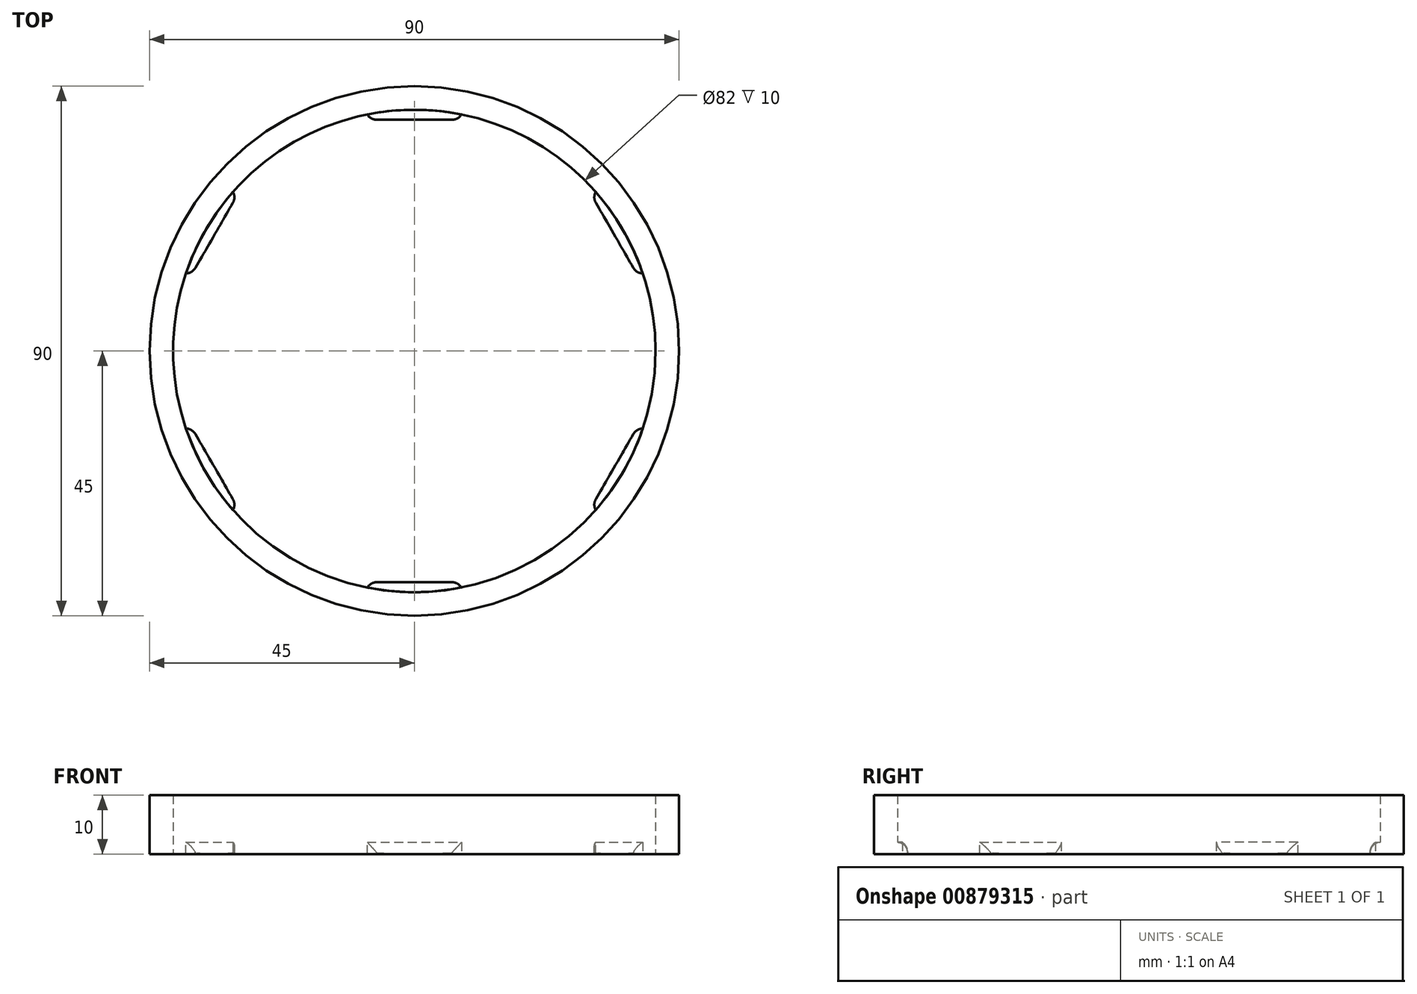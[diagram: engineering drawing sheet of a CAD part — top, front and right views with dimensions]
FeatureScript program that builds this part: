
annotation { "Feature Type Name" : "Feature", "Feature Type Description" : "" }
export const myFeature = defineFeature(function(context is Context, id is Id, definition is map)
    precondition{}
    {
        {
            var Q0;
            Q0=qCreatedBy(makeId("Top.planeOp"),FACE);
            var sketch = newSketch(context, id + "F0", { "sketchPlane" : qUnion([Q0])});
            skCircle(sketch, "E0", {"center": v(0, 0) * mm, "radius": 41 * mm});
            skLineSegment(sketch, "E1.top", {"start": v(30.03, 26.58) * mm, "end": v(34.03, 19.65) * mm});
            skPoint(sketch, "E1.middle", {"position": v(35.5, 20.5) * mm});
            skLineSegment(sketch, "E2", {"start": v(30.03, 26.58) * mm, "end": v(30.82, 27.03) * mm});
            skLineSegment(sketch, "E3.MirrorCS", {"start": v(38.03, 12.72) * mm, "end": v(38.82, 13.18) * mm});
            skLineSegment(sketch, "E4.MirrorCS", {"start": v(38.03, 12.72) * mm, "end": v(34.03, 19.65) * mm});
            skLineSegment(sketch, "E5.1.0", {"start": v(-8, 39.3) * mm, "end": v(-8, 40.21) * mm});
            skLineSegment(sketch, "E5.1.1", {"start": v(-8, 39.3) * mm, "end": v(0, 39.3) * mm});
            skLineSegment(sketch, "E5.1.2", {"start": v(8, 39.3) * mm, "end": v(0, 39.3) * mm});
            skLineSegment(sketch, "E5.1.3", {"start": v(8, 39.3) * mm, "end": v(8, 40.21) * mm});
            skLineSegment(sketch, "E5.2.0", {"start": v(-38.03, 12.72) * mm, "end": v(-38.82, 13.18) * mm});
            skLineSegment(sketch, "E5.2.1", {"start": v(-38.03, 12.72) * mm, "end": v(-34.03, 19.65) * mm});
            skLineSegment(sketch, "E5.2.2", {"start": v(-30.03, 26.58) * mm, "end": v(-34.03, 19.65) * mm});
            skLineSegment(sketch, "E5.2.3", {"start": v(-30.03, 26.58) * mm, "end": v(-30.82, 27.03) * mm});
            skLineSegment(sketch, "E5.3.0", {"start": v(-30.03, -26.58) * mm, "end": v(-30.82, -27.03) * mm});
            skLineSegment(sketch, "E5.3.1", {"start": v(-30.03, -26.58) * mm, "end": v(-34.03, -19.65) * mm});
            skLineSegment(sketch, "E5.3.2", {"start": v(-38.03, -12.72) * mm, "end": v(-34.03, -19.65) * mm});
            skLineSegment(sketch, "E5.3.3", {"start": v(-38.03, -12.72) * mm, "end": v(-38.82, -13.18) * mm});
            skLineSegment(sketch, "E5.4.0", {"start": v(8, -39.3) * mm, "end": v(8, -40.21) * mm});
            skLineSegment(sketch, "E5.4.1", {"start": v(8, -39.3) * mm, "end": v(0, -39.3) * mm});
            skLineSegment(sketch, "E5.4.2", {"start": v(-8, -39.3) * mm, "end": v(0, -39.3) * mm});
            skLineSegment(sketch, "E5.4.3", {"start": v(-8, -39.3) * mm, "end": v(-8, -40.21) * mm});
            skLineSegment(sketch, "E5.5.0", {"start": v(38.03, -12.72) * mm, "end": v(38.82, -13.18) * mm});
            skLineSegment(sketch, "E5.5.1", {"start": v(38.03, -12.72) * mm, "end": v(34.03, -19.65) * mm});
            skLineSegment(sketch, "E5.5.2", {"start": v(30.03, -26.58) * mm, "end": v(34.03, -19.65) * mm});
            skLineSegment(sketch, "E5.5.3", {"start": v(30.03, -26.58) * mm, "end": v(30.82, -27.03) * mm});
            skCircle(sketch, "E6", {"center": v(0, 0) * mm, "radius": 45 * mm});
            skSolve(sketch);
        }
        {
            var Q0;
            Q0=makeQuery(id+"F0.imprint","IMPRINT",FACE,{"disambiguationData":[TD([[makeQuery(id+"F0.imprint","IMPRINT",EDGE,{"derivedFrom":sQuery(id+"F0.wireOp",EDGE,"E6")}),1.0]])]});
            extrude(context, id + "F1", {"entities" : qUnion([Q0]), "depth" : 10 * mm, "offsetDistance" : 25 * mm});
        }
        {
            var Q0;
            {var subQ0=sQuery(id+"F0.wireOp",EDGE,"E5.1.0");Q0=makeQuery(id+"F0.imprint","IMPRINT",FACE,{"disambiguationData":[TD([[makeQuery(id+"F0.imprint","IMPRINT",EDGE,{"derivedFrom":subQ0}),-1.0]])]});}
            var Q1;
            {var subQ0=sQuery(id+"F0.wireOp",EDGE,"E5.2.0");Q1=makeQuery(id+"F0.imprint","IMPRINT",FACE,{"disambiguationData":[TD([[makeQuery(id+"F0.imprint","IMPRINT",EDGE,{"derivedFrom":subQ0}),-1.0]])]});}
            var Q2;
            Q2=makeQuery(id+"F0.imprint","IMPRINT",FACE,{"disambiguationData":[TD([[makeQuery(id+"F0.imprint","IMPRINT",EDGE,{"derivedFrom":sQuery(id+"F0.wireOp",EDGE,"E1.top")}),1.0]])]});
            var Q3;
            {var subQ0=sQuery(id+"F0.wireOp",EDGE,"E5.5.0");Q3=makeQuery(id+"F0.imprint","IMPRINT",FACE,{"disambiguationData":[TD([[makeQuery(id+"F0.imprint","IMPRINT",EDGE,{"derivedFrom":subQ0}),-1.0]])]});}
            var Q4;
            {var subQ0=sQuery(id+"F0.wireOp",EDGE,"E5.4.0");Q4=makeQuery(id+"F0.imprint","IMPRINT",FACE,{"disambiguationData":[TD([[makeQuery(id+"F0.imprint","IMPRINT",EDGE,{"derivedFrom":subQ0}),-1.0]])]});}
            var Q5;
            {var subQ0=sQuery(id+"F0.wireOp",EDGE,"E5.3.0");Q5=makeQuery(id+"F0.imprint","IMPRINT",FACE,{"disambiguationData":[TD([[makeQuery(id+"F0.imprint","IMPRINT",EDGE,{"derivedFrom":subQ0}),-1.0]])]});}
            extrude(context, id + "F2", {"entities" : qUnion([Q0, Q1, Q2, Q3, Q4, Q5]), "operationType" : NewBodyOperationType.ADD, "depth" : 2 * mm, "offsetDistance" : 25 * mm});
        }
        {
            var Q0;
            Q0=makeQuery(id+"F2.opExtrude","CAP_EDGE",EDGE,{"disambiguationData":[OSD([sQuery(id+"F0.wireOp",EDGE,"E5.1.1"),sQuery(id+"F0.wireOp",EDGE,"E5.1.2")])],"isStart":false});
            var Q1;
            Q1=makeQuery(id+"F2.opExtrude","SWEPT_EDGE",EDGE,{"disambiguationData":[OSD([sQuery(id+"F0.wireOp",EDGE,"E5.1.2"),sQuery(id+"F0.wireOp",EDGE,"E5.1.3")])]});
            var Q2;
            Q2=makeQuery(id+"F2.opExtrude","SWEPT_EDGE",EDGE,{"disambiguationData":[OSD([sQuery(id+"F0.wireOp",EDGE,"E5.1.0"),sQuery(id+"F0.wireOp",EDGE,"E5.1.1")])]});
            fillet(context, id + "F3", {"entities" : qUnion([Q0, Q1, Q2]), "radius" : 2 * mm, "tangentPropagation" : true, "rho" : 0.5, "crossSection" : FilletCrossSection.CONIC, "allowEdgeOverflow" : false});
        }
        {
            var Q0;
            Q0=makeQuery(id+"F2.opExtrude","CAP_EDGE",EDGE,{"disambiguationData":[OSD([sQuery(id+"F0.wireOp",EDGE,"E5.2.1"),sQuery(id+"F0.wireOp",EDGE,"E5.2.2")])],"isStart":false});
            var Q1;
            Q1=makeQuery(id+"F2.opExtrude","SWEPT_EDGE",EDGE,{"disambiguationData":[OSD([sQuery(id+"F0.wireOp",EDGE,"E5.2.0"),sQuery(id+"F0.wireOp",EDGE,"E5.2.1")])]});
            var Q2;
            Q2=makeQuery(id+"F2.opExtrude","SWEPT_EDGE",EDGE,{"disambiguationData":[OSD([sQuery(id+"F0.wireOp",EDGE,"E5.2.2"),sQuery(id+"F0.wireOp",EDGE,"E5.2.3")])]});
            fillet(context, id + "F4", {"entities" : qUnion([Q0, Q1, Q2]), "radius" : 2 * mm, "tangentPropagation" : true, "rho" : 0.5, "crossSection" : FilletCrossSection.CONIC, "allowEdgeOverflow" : false});
        }
        {
            var Q0;
            Q0=makeQuery(id+"F2.opExtrude","CAP_EDGE",EDGE,{"disambiguationData":[OSD([sQuery(id+"F0.wireOp",EDGE,"E5.3.1"),sQuery(id+"F0.wireOp",EDGE,"E5.3.2")])],"isStart":false});
            var Q1;
            Q1=makeQuery(id+"F2.opExtrude","SWEPT_EDGE",EDGE,{"disambiguationData":[OSD([sQuery(id+"F0.wireOp",EDGE,"E5.3.0"),sQuery(id+"F0.wireOp",EDGE,"E5.3.1")])]});
            var Q2;
            Q2=makeQuery(id+"F2.opExtrude","SWEPT_EDGE",EDGE,{"disambiguationData":[OSD([sQuery(id+"F0.wireOp",EDGE,"E5.3.2"),sQuery(id+"F0.wireOp",EDGE,"E5.3.3")])]});
            fillet(context, id + "F5", {"entities" : qUnion([Q0, Q1, Q2]), "radius" : 2 * mm, "tangentPropagation" : true, "rho" : 0.5, "crossSection" : FilletCrossSection.CONIC, "allowEdgeOverflow" : false});
        }
        {
            var Q0;
            Q0=makeQuery(id+"F2.opExtrude","CAP_EDGE",EDGE,{"disambiguationData":[OSD([sQuery(id+"F0.wireOp",EDGE,"E5.4.1"),sQuery(id+"F0.wireOp",EDGE,"E5.4.2")])],"isStart":false});
            var Q1;
            Q1=makeQuery(id+"F2.opExtrude","SWEPT_EDGE",EDGE,{"disambiguationData":[OSD([sQuery(id+"F0.wireOp",EDGE,"E5.4.2"),sQuery(id+"F0.wireOp",EDGE,"E5.4.3")])]});
            var Q2;
            Q2=makeQuery(id+"F2.opExtrude","SWEPT_EDGE",EDGE,{"disambiguationData":[OSD([sQuery(id+"F0.wireOp",EDGE,"E5.4.0"),sQuery(id+"F0.wireOp",EDGE,"E5.4.1")])]});
            fillet(context, id + "F6", {"entities" : qUnion([Q0, Q1, Q2]), "radius" : 2 * mm, "tangentPropagation" : true, "rho" : 0.5, "crossSection" : FilletCrossSection.CONIC, "allowEdgeOverflow" : false});
        }
        {
            var Q0;
            Q0=makeQuery(id+"F2.opExtrude","CAP_EDGE",EDGE,{"disambiguationData":[OSD([sQuery(id+"F0.wireOp",EDGE,"E5.5.1"),sQuery(id+"F0.wireOp",EDGE,"E5.5.2")])],"isStart":false});
            var Q1;
            Q1=makeQuery(id+"F2.opExtrude","SWEPT_EDGE",EDGE,{"disambiguationData":[OSD([sQuery(id+"F0.wireOp",EDGE,"E5.5.2"),sQuery(id+"F0.wireOp",EDGE,"E5.5.3")])]});
            var Q2;
            Q2=makeQuery(id+"F2.opExtrude","SWEPT_EDGE",EDGE,{"disambiguationData":[OSD([sQuery(id+"F0.wireOp",EDGE,"E5.5.0"),sQuery(id+"F0.wireOp",EDGE,"E5.5.1")])]});
            fillet(context, id + "F7", {"entities" : qUnion([Q0, Q1, Q2]), "radius" : 2 * mm, "tangentPropagation" : true, "rho" : 0.5, "crossSection" : FilletCrossSection.CONIC, "allowEdgeOverflow" : false});
        }
        {
            var Q0;
            Q0=makeQuery(id+"F2.opExtrude","CAP_EDGE",EDGE,{"disambiguationData":[OSD([sQuery(id+"F0.wireOp",EDGE,"E1.top"),sQuery(id+"F0.wireOp",EDGE,"E4.MirrorCS")])],"isStart":false});
            var Q1;
            Q1=makeQuery(id+"F2.opExtrude","SWEPT_EDGE",EDGE,{"disambiguationData":[OSD([sQuery(id+"F0.wireOp",EDGE,"E1.top"),sQuery(id+"F0.wireOp",EDGE,"E2")])]});
            var Q2;
            Q2=makeQuery(id+"F2.opExtrude","SWEPT_EDGE",EDGE,{"disambiguationData":[OSD([sQuery(id+"F0.wireOp",EDGE,"E3.MirrorCS"),sQuery(id+"F0.wireOp",EDGE,"E4.MirrorCS")])]});
            fillet(context, id + "F8", {"entities" : qUnion([Q0, Q1, Q2]), "radius" : 2 * mm, "tangentPropagation" : true, "rho" : 0.5, "crossSection" : FilletCrossSection.CONIC, "allowEdgeOverflow" : false});
        }
    });
